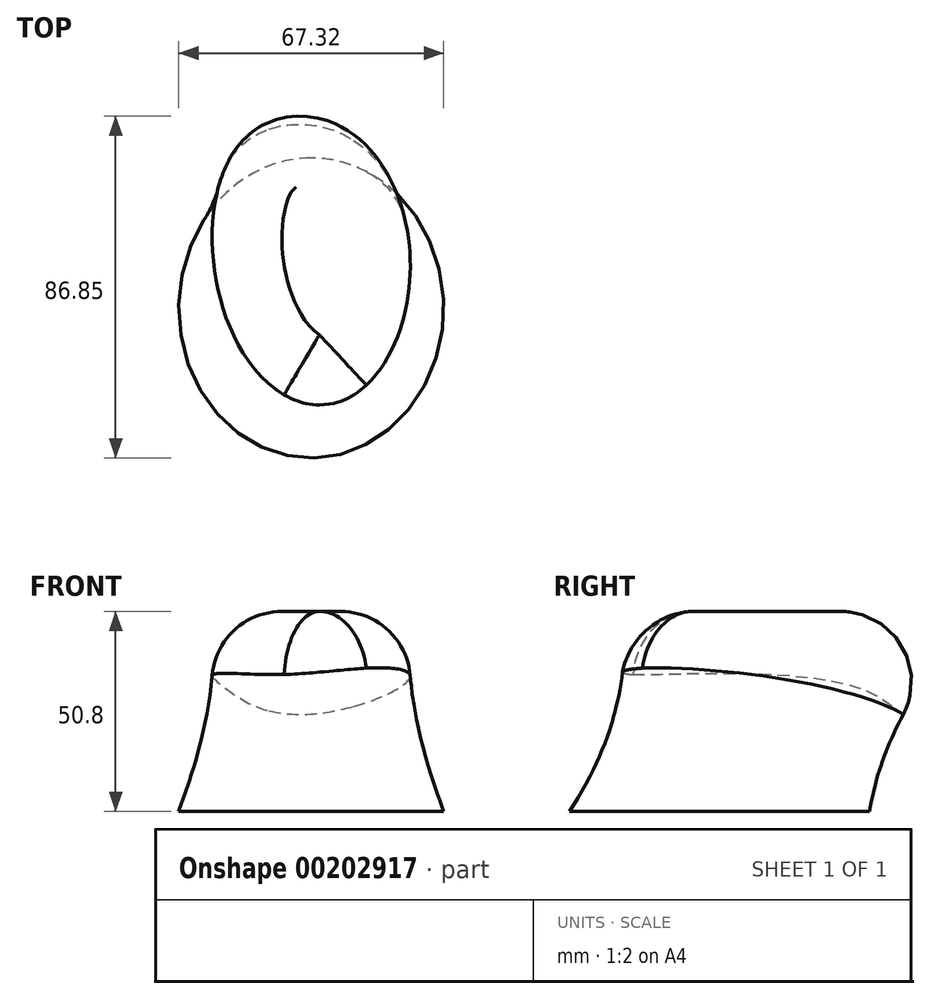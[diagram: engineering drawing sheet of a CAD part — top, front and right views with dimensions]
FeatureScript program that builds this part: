
annotation { "Feature Type Name" : "Feature", "Feature Type Description" : "" }
export const myFeature = defineFeature(function(context is Context, id is Id, definition is map)
    precondition{}
    {
        {
            var Q0;
            Q0=qCreatedBy(makeId("Top.planeOp"),FACE);
            var sketch = newSketch(context, id + "F0", { "sketchPlane" : qUnion([Q0])});
            skEllipse(sketch, "E0", {"center": v(0, 0) * mm, "majorRadius": 38.1 * mm, "minorRadius": 33.66 * mm, "majorAxis": v(0, 1)});
            skSolve(sketch);
        }
        {
            var Q0;
            Q0=qCreatedBy(makeId("Top.planeOp"),FACE);
            cPlane(context, id + "F1", {"entities" : qUnion([Q0]), "cplaneType" : CPlaneType.OFFSET, "offset" : 50.8 * mm, "width" : 152.4 * mm, "height" : 152.4 * mm});
        }
        {
            var Q0;
            Q0=qCreatedBy(id+"F1.planeOp",FACE);
            var sketch = newSketch(context, id + "F2", { "sketchPlane" : qUnion([Q0])});
            skEllipse(sketch, "E1", {"center": v(0, 20.5) * mm, "majorRadius": 25.4 * mm, "minorRadius": 44.45 * mm, "majorAxis": v(1, 0)});
            skSolve(sketch);
        }
        {
            var Q0;
            Q0=makeQuery(id+"F0.imprint","IMPRINT",FACE,{"disambiguationData":[TD([[makeQuery(id+"F0.imprint","IMPRINT",EDGE,{"derivedFrom":sQuery(id+"F0.wireOp",EDGE,"E0")}),1.0]])]});
            var Q1;
            Q1=makeQuery(id+"F2.imprint","IMPRINT",FACE,{"disambiguationData":[TD([[makeQuery(id+"F2.imprint","IMPRINT",EDGE,{"derivedFrom":sQuery(id+"F2.wireOp",EDGE,"E1")}),1.0]])]});
            loft(context, id + "F3", {"sheetProfilesArray" : [{ "sheetProfileEntities" : qUnion([Q0]) }, { "sheetProfileEntities" : qUnion([Q1]) }]});
        }
        {
            var Q0;
            Q0=makeQuery(id+"F3.opLoft","MID_CAP_EDGE",EDGE,{"disambiguationData":[OSD([sQuery(id+"F0.wireOp",EDGE,"E0"),sQuery(id+"F2.wireOp",EDGE,"E1")])],"capPos":1.0});
            fillet(context, id + "F4", {"entities" : qUnion([Q0]), "radius" : 17.78 * mm, "tangentPropagation" : true, "allowEdgeOverflow" : false});
        }
    });
